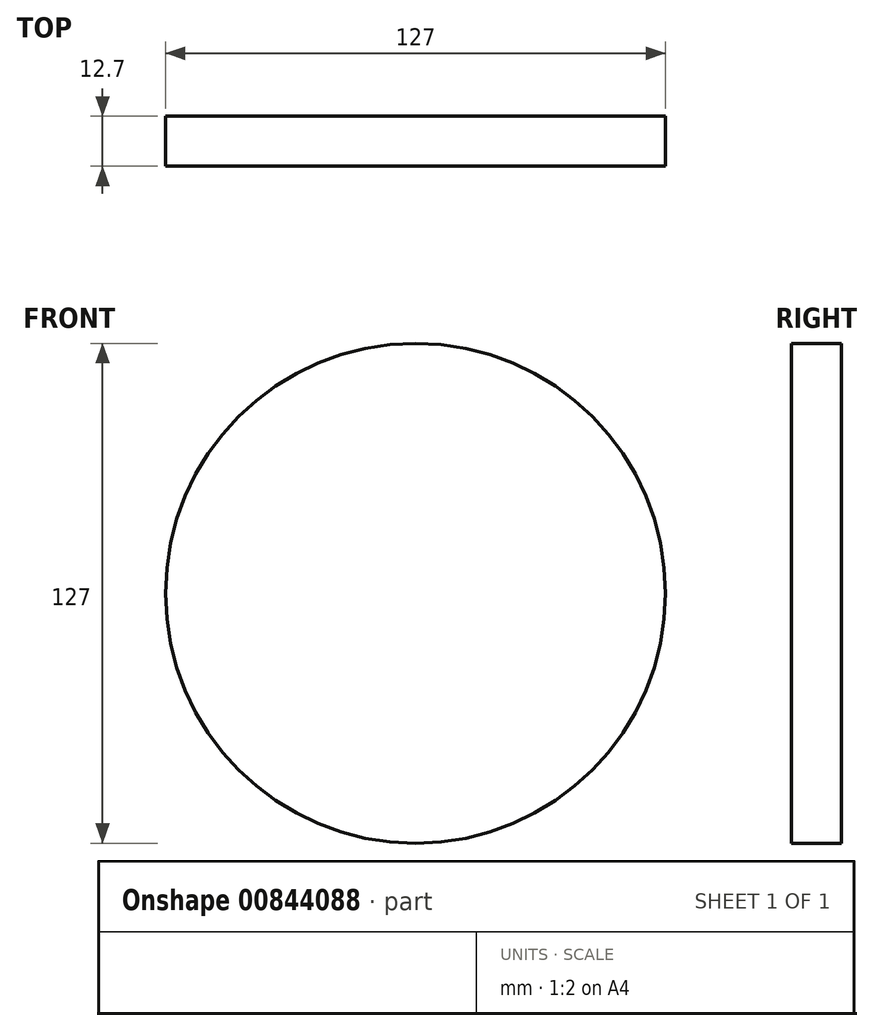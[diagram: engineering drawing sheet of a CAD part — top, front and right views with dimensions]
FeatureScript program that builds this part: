
annotation { "Feature Type Name" : "Feature", "Feature Type Description" : "" }
export const myFeature = defineFeature(function(context is Context, id is Id, definition is map)
    precondition{}
    {
        {
            var Q0;
            Q0=qCreatedBy(makeId("Front.planeOp"),FACE);
            var sketch = newSketch(context, id + "F0", { "sketchPlane" : qUnion([Q0])});
            skCircle(sketch, "E0", {"center": v(0, 0) * mm, "radius": 63.5 * mm});
            skSolve(sketch);
        }
        {
            var Q0;
            Q0 = qSketchRegion(id + "F0", true);
            extrude(context, id + "F1", {"entities" : qUnion([Q0]), "depth" : 12.7 * mm, "offsetDistance" : 25.4 * mm});
        }
        {
            var Q0;
            Q0=qCreatedBy(makeId("Front.planeOp"),FACE);
            var sketch = newSketch(context, id + "F2", { "sketchPlane" : qUnion([Q0])});
            skCircle(sketch, "E1", {"center": v(-38.67, 38.67) * mm, "radius": 6.35 * mm});
            skCircle(sketch, "E2.1.0", {"center": v(-38.67, -38.67) * mm, "radius": 6.35 * mm});
            skCircle(sketch, "E2.2.0", {"center": v(38.67, -38.67) * mm, "radius": 6.35 * mm});
            skCircle(sketch, "E2.3.0", {"center": v(38.67, 38.67) * mm, "radius": 6.35 * mm});
            skPoint(sketch, "E2.center", {"position": v(0, 0) * mm});
            skSolve(sketch);
        }
        {
            var Q0;
            Q0 = qConstructionFilter(qBodyType(qCreatedBy(id + "F2" ,EDGE), BodyType.WIRE), ConstructionObject.NO);
            extrude(context, id + "F3", {"bodyType" : ToolBodyType.SURFACE, "surfaceEntities" : qUnion([Q0]), "depth" : 12.7 * mm, "offsetDistance" : 25.4 * mm});
        }
    });
